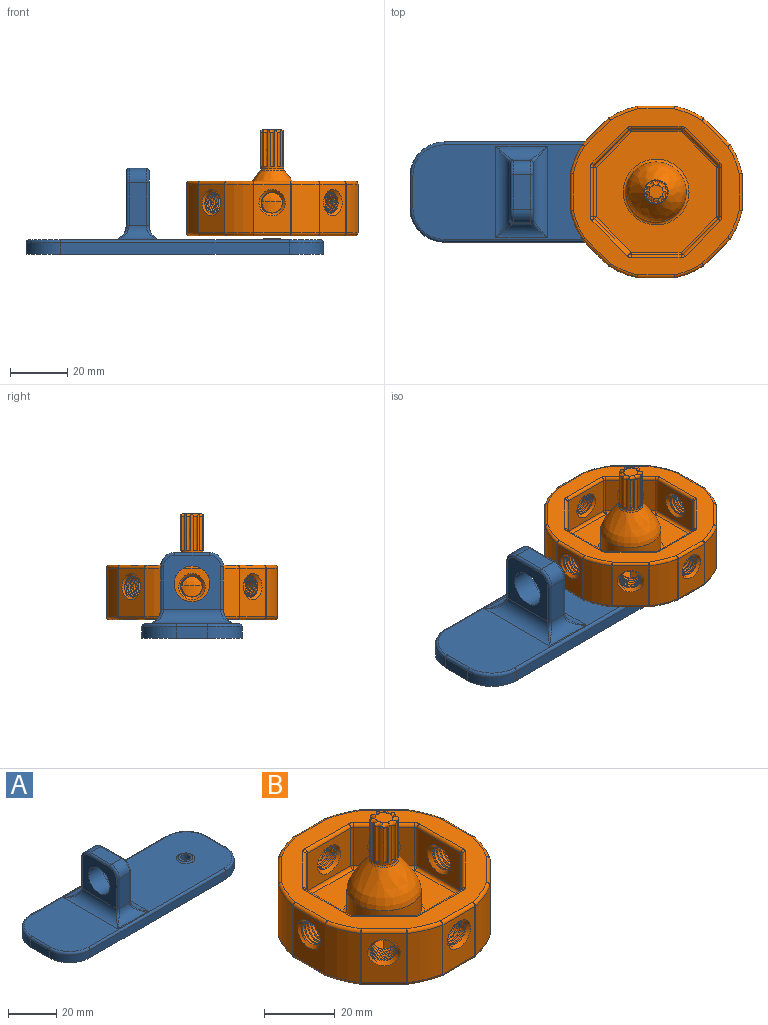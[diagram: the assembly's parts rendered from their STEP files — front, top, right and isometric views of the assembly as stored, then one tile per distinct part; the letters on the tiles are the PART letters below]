
ASSEMBLY  parts=2 mates=1
PART A: 49 faces, bbox 106x37x30.4 mm
  f0: plane 80x4mm, normal (0,1,0), area 320mm2, adj f1,f7,f10,f47
  f1: cylinder r=12mm len=12mm, axis (0,0,-1), area 75.4mm2, adj f0,f2,f10,f45
  f2: plane 11x4mm, normal (-1,0,0), area 44mm2, adj f1,f3,f10,f43
  f3: cylinder r=12mm len=12mm, axis (0,0,-1), area 75.4mm2, adj f2,f4,f10,f41
  f4: plane 80x4mm, normal (0,-1,0), area 320mm2, adj f3,f5,f10,f42
  f5: cylinder r=12mm len=12mm, axis (0,0,-1), area 75.4mm2, adj f4,f6,f10,f44
  f6: plane 11x4mm, normal (1,0,0), area 44mm2, adj f5,f7,f10,f46
  f7: cylinder r=12mm len=12mm, axis (0,0,-1), area 75.4mm2, adj f0,f6,f10,f48
  f8: cylinder r=2mm len=4mm, axis (0,0,-1), area 31.4mm2, adj f11,f13
  f9: plane 102x33mm, normal (0,0,1), area 2639.2mm2, adj f20,f21,f22,f23,f40,f41,f42,f43
  f10: plane 104x35mm, normal (0,0,-1), area 3477.9mm2, adj f0,f1,f2,f3,f4,f5,f6,f7
  f11: plane 6x6mm, normal (0,0,1), area 15.7mm2, adj f8,f40
  f12: cylinder r=3.5mm len=7mm, axis (0,0,-1), area 66mm2, adj f10,f13
  f13: plane 7x7mm, normal (0,0,-1), area 25.9mm2, adj f8,f12
  f14: plane 15x6mm, normal (0,1,0), area 90mm2, adj f23,f25,f31,f38
  f15: plane 20x19mm, normal (-1,0,0), area 250.4mm2, adj f19,f22,f34,f35,f36,f37,f38
  f16: plane 15x6mm, normal (0,-1,0), area 90mm2, adj f20,f24,f27,f34
  f17: plane 20x19mm, normal (1,0,0), area 250.4mm2, adj f19,f21,f27,f28,f29,f30,f31
  f18: plane 12x6mm, normal (0,0,1), area 72mm2, adj f24,f25,f29,f36
  f19: cylinder r=6.25mm len=12.5mm, axis (-1,0,0), area 314.2mm2, adj f15,f17
  f20: cylinder r=5mm len=18mm, axis (-1,0,0), area 81.4mm2, adj f9,f16,f26,f33
  f21: cylinder r=5mm len=32mm, axis (0,-1,0), area 191.3mm2, adj f9,f17,f26,f32
  f22: cylinder r=5mm len=32mm, axis (0,1,0), area 191.3mm2, adj f9,f15,f33,f39
  f23: cylinder r=5mm len=18mm, axis (1,0,0), area 81.4mm2, adj f9,f14,f32,f39
  f24: cylinder r=5mm len=6mm, axis (-1,0,0), area 47.1mm2, adj f16,f18,f28,f35
  f25: cylinder r=5mm len=6mm, axis (1,0,0), area 47.1mm2, adj f14,f18,f30,f37
  f26: bspline ~6x6mm, area 8.8mm2, adj f20,f21,f27
  f27: cylinder r=1mm len=15mm, axis (0,0,1), area 23.6mm2, adj f16,f17,f26,f28
  f28: torus R=4mm, axis (1,0,0), area 11.4mm2, adj f17,f24,f27,f29
  f29: cylinder r=1mm len=12mm, axis (0,-1,0), area 18.8mm2, adj f17,f18,f28,f30
  f30: torus R=4mm, axis (1,0,0), area 11.4mm2, adj f17,f25,f29,f31
  f31: cylinder r=1mm len=15mm, axis (0,0,-1), area 23.6mm2, adj f14,f17,f30,f32
  f32: bspline ~6x6mm, area 8.8mm2, adj f21,f23,f31
  f33: bspline ~6x6mm, area 8.8mm2, adj f20,f22,f34
  f34: cylinder r=1mm len=15mm, axis (0,0,-1), area 23.6mm2, adj f15,f16,f33,f35
  f35: torus R=4mm, axis (1,0,0), area 11.4mm2, adj f15,f24,f34,f36
  f36: cylinder r=1mm len=12mm, axis (0,1,0), area 18.8mm2, adj f15,f18,f35,f37
  f37: torus R=4mm, axis (1,0,0), area 11.4mm2, adj f15,f25,f36,f38
  f38: cylinder r=1mm len=15mm, axis (0,0,1), area 23.6mm2, adj f14,f15,f37,f39
  f39: bspline ~6x6mm, area 8.8mm2, adj f22,f23,f38
  f40: torus R=3.87mm, axis (0,0,1), area 22.3mm2, adj f9,f11
  f41: torus R=11mm, axis (0,0,1), area 28.7mm2, adj f3,f9,f42,f43
  f42: cylinder r=1mm len=80mm, axis (-1,0,0), area 125.7mm2, adj f4,f9,f41,f44
  f43: cylinder r=1mm len=11mm, axis (0,1,0), area 17.3mm2, adj f2,f9,f41,f45
  f44: torus R=11mm, axis (0,0,1), area 28.7mm2, adj f5,f9,f42,f46
  f45: torus R=11mm, axis (0,0,1), area 28.7mm2, adj f1,f9,f43,f47
  f46: cylinder r=1mm len=11mm, axis (0,-1,0), area 17.3mm2, adj f6,f9,f44,f48
  f47: cylinder r=1mm len=80mm, axis (1,0,0), area 125.7mm2, adj f0,f9,f45,f48
  f48: torus R=11mm, axis (0,0,1), area 28.7mm2, adj f7,f9,f46,f47
PART B: 228 faces, bbox 60.9x60.9x37 mm
  f0: cylinder r=4mm len=13.49mm, axis (0,0,1), area 145.4mm2, adj f75,f76,f77,f78,f79,f80,f81,f82
  f1: plane 17.4x13mm, normal (0,-1,0), area 159.7mm2, adj f11,f133,f134,f142,f143
  f2: cylinder r=30.7mm len=17mm, axis (0,0,-1), area 183.4mm2, adj f195,f200,f204,f205
  f3: plane 17x12.78mm, normal (0,1,0), area 150.9mm2, adj f10,f205,f210,f214,f215
  f4: cylinder r=30.7mm len=17mm, axis (0,0,-1), area 183.4mm2, adj f215,f220,f223,f226
  f5: plane 58x58mm, normal (0,0,1), area 970.6mm2, adj f107,f108,f109,f111,f112,f116,f117,f121
  f6: plane 58x58mm, normal (0,0,-1), area 2546.2mm2, adj f153,f154,f163,f164,f173,f174,f183,f184
  f7: cylinder r=6.5mm len=13mm, axis (0,0,-1), area 122.5mm2, adj f74,f227
  f8: plane 42x42mm, normal (0,0,1), area 1045.9mm2, adj f105,f114,f119,f124,f129,f135,f140,f143
  f9: cylinder r=3.6mm len=7.2mm, axis (0,-1,0), area 84.6mm2, adj f10,f11,f12,f13
  f10: cone r=3.6mm half-angle=45deg, axis (0,1,0), area 33.9mm2, adj f3,f9,f12,f13
  f11: cone r=4.6mm half-angle=45deg, axis (0,-1,0), area 33.9mm2, adj f1,f9,f12,f13
  f12: bspline ~8.17x8.17mm, area 57.8mm2, adj f9,f10,f11,f13
  f13: bspline ~8.17x8.17mm, area 57.8mm2, adj f9,f10,f11,f12
  f14: plane 13x12.3mm, normal (-0.71,-0.71,0), area 159.7mm2, adj f19,f122,f123,f134,f135
  f15: cylinder r=30.7mm len=17mm, axis (0,0,-1), area 183.4mm2, adj f175,f180,f184,f185
  f16: plane 17x9.04mm, normal (0.71,0.71,0), area 150.9mm2, adj f18,f185,f190,f194,f195
  f17: cylinder r=3.6mm len=9.33mm, axis (-0.71,-0.71,0), area 84.6mm2, adj f18,f19,f20,f21
  f18: cone r=3.6mm half-angle=45deg, axis (0.71,0.71,0), area 33.9mm2, adj f16,f17,f20,f21
  f19: cone r=4.6mm half-angle=45deg, axis (-0.71,-0.71,0), area 33.9mm2, adj f14,f17,f20,f21
  f20: bspline ~9.75x9.75mm, area 57.8mm2, adj f17,f18,f19,f21
  f21: bspline ~9.75x9.75mm, area 57.8mm2, adj f17,f18,f19,f20
  f22: plane 17.4x13mm, normal (-1,0,0), area 159.7mm2, adj f27,f112,f113,f123,f124
  f23: cylinder r=30.7mm len=17mm, axis (0,0,-1), area 183.4mm2, adj f155,f160,f164,f165
  f24: plane 17x12.78mm, normal (1,0,0), area 150.9mm2, adj f26,f165,f170,f174,f175
  f25: cylinder r=3.6mm len=7.2mm, axis (-1,0,0), area 84.6mm2, adj f26,f27,f28,f29
  f26: cone r=3.6mm half-angle=45deg, axis (1,0,0), area 33.9mm2, adj f24,f25,f28,f29
  f27: cone r=4.6mm half-angle=45deg, axis (-1,0,0), area 33.9mm2, adj f22,f25,f28,f29
  f28: bspline ~8.17x8.17mm, area 57.8mm2, adj f25,f26,f27,f29
  f29: bspline ~8.17x8.17mm, area 57.8mm2, adj f25,f26,f27,f28
  f30: plane 13x12.3mm, normal (-0.71,0.71,0), area 159.7mm2, adj f35,f107,f110,f113,f114
  f31: cylinder r=30.7mm len=17mm, axis (0,0,-1), area 183.4mm2, adj f147,f151,f152,f153
  f32: plane 17x9.04mm, normal (0.71,-0.71,0), area 150.9mm2, adj f34,f147,f150,f154,f155
  f33: cylinder r=3.6mm len=9.33mm, axis (-0.71,0.71,0), area 84.6mm2, adj f34,f35,f36,f37
  f34: cone r=3.6mm half-angle=45deg, axis (0.71,-0.71,0), area 33.9mm2, adj f32,f33,f36,f37
  f35: cone r=4.6mm half-angle=45deg, axis (-0.71,0.71,0), area 33.9mm2, adj f30,f33,f36,f37
  f36: bspline ~9.75x9.75mm, area 57.8mm2, adj f33,f34,f35,f37
  f37: bspline ~9.75x9.75mm, area 57.8mm2, adj f33,f34,f35,f36
  f38: plane 17.4x13mm, normal (0,1,0), area 159.7mm2, adj f43,f110,f111,f119,f120
  f39: cylinder r=30.7mm len=17mm, axis (0,0,-1), area 183.4mm2, adj f162,f171,f172,f173
  f40: plane 17x12.78mm, normal (0,-1,0), area 150.9mm2, adj f42,f152,f161,f162,f163
  f41: cylinder r=3.6mm len=7.2mm, axis (0,1,0), area 84.6mm2, adj f42,f43,f44,f45
  f42: cone r=3.6mm half-angle=45deg, axis (0,-1,0), area 33.9mm2, adj f40,f41,f44,f45
  f43: cone r=4.6mm half-angle=45deg, axis (0,1,0), area 33.9mm2, adj f38,f41,f44,f45
  f44: bspline ~8.17x8.17mm, area 57.8mm2, adj f41,f42,f43,f45
  f45: bspline ~8.17x8.17mm, area 57.8mm2, adj f41,f42,f43,f44
  f46: plane 13x12.3mm, normal (0.71,0.71,0), area 159.7mm2, adj f51,f120,f121,f129,f130
  f47: cylinder r=30.7mm len=17mm, axis (0,0,-1), area 183.4mm2, adj f182,f191,f192,f193
  f48: plane 17x9.04mm, normal (-0.71,-0.71,0), area 150.9mm2, adj f50,f172,f181,f182,f183
  f49: cylinder r=3.6mm len=9.33mm, axis (0.71,0.71,0), area 84.6mm2, adj f50,f51,f52,f53
  f50: cone r=3.6mm half-angle=45deg, axis (-0.71,-0.71,0), area 33.9mm2, adj f48,f49,f52,f53
  f51: cone r=4.6mm half-angle=45deg, axis (0.71,0.71,0), area 33.9mm2, adj f46,f49,f52,f53
  f52: bspline ~9.75x9.75mm, area 57.8mm2, adj f49,f50,f51,f53
  f53: bspline ~9.75x9.75mm, area 57.8mm2, adj f49,f50,f51,f52
  f54: plane 17.4x13mm, normal (1,0,0), area 159.7mm2, adj f59,f130,f131,f140,f141
  f55: cylinder r=30.7mm len=17mm, axis (0,0,-1), area 183.4mm2, adj f202,f211,f212,f213
  f56: plane 17x12.78mm, normal (-1,0,0), area 150.9mm2, adj f58,f192,f201,f202,f203
  f57: cylinder r=3.6mm len=7.2mm, axis (1,0,0), area 84.6mm2, adj f58,f59,f60,f61
  f58: cone r=3.6mm half-angle=45deg, axis (-1,0,0), area 33.9mm2, adj f56,f57,f60,f61
  f59: cone r=4.6mm half-angle=45deg, axis (1,0,0), area 33.9mm2, adj f54,f57,f60,f61
  f60: bspline ~8.17x8.17mm, area 57.8mm2, adj f57,f58,f59,f61
  f61: bspline ~8.17x8.17mm, area 57.8mm2, adj f57,f58,f59,f60
  f62: plane 13x12.3mm, normal (0.71,-0.71,0), area 159.7mm2, adj f66,f132,f141,f142,f146
  f63: plane 17x9.04mm, normal (-0.71,0.71,0), area 150.9mm2, adj f65,f212,f221,f222,f226
  f64: cylinder r=3.6mm len=9.33mm, axis (0.71,-0.71,0), area 84.6mm2, adj f65,f66,f67,f68
  f65: cone r=3.6mm half-angle=45deg, axis (-0.71,0.71,0), area 33.9mm2, adj f63,f64,f67,f68
  f66: cone r=4.6mm half-angle=45deg, axis (0.71,-0.71,0), area 33.9mm2, adj f62,f64,f67,f68
  f67: bspline ~9.75x9.75mm, area 57.8mm2, adj f64,f65,f66,f68
  f68: bspline ~9.75x9.75mm, area 57.8mm2, adj f64,f65,f66,f67
  f69: plane 5.51x5.24mm, normal (0,0,1), area 19.2mm2, adj f95,f96,f97,f98,f99,f100,f101,f102
  f70: revolved ~21x21mm, area 619.2mm2, adj f71,f106
  f71: cylinder r=10.5mm len=21mm, axis (0,0,1), area 468.7mm2, adj f70,f105
  f72: cone r=0mm half-angle=31.2deg, axis (0,0,-1), area 193.9mm2, adj f73
  f73: cylinder r=5.65mm len=11.3mm, axis (0,0,1), area 277mm2, adj f72,f74
  f74: cone r=5.65mm half-angle=45deg, axis (0,0,-1), area 45.9mm2, adj f7,f73
  f75: extruded ~12x1.39mm, area 23.3mm2, adj f0,f76,f100
  f76: plane 1.39x0.99mm, normal (0,0,1), area 0.6mm2, adj f0,f75
  f77: extruded ~12x1.19mm, area 23.3mm2, adj f0,f78,f104
  f78: plane 1.27x1.21mm, normal (0,0,1), area 0.6mm2, adj f0,f77
  f79: extruded ~12x1.39mm, area 23.3mm2, adj f0,f80,f102
  f80: plane 1.39x0.99mm, normal (0,0,1), area 0.6mm2, adj f0,f79
  f81: extruded ~12x1.19mm, area 23.3mm2, adj f0,f82,f98
  f82: plane 1.27x1.21mm, normal (0,0,1), area 0.6mm2, adj f0,f81
  f83: extruded ~12x1.46mm, area 23.3mm2, adj f0,f84,f96
  f84: plane 1.46x0.86mm, normal (0,0,1), area 0.6mm2, adj f0,f83
  f85: extruded ~12x1.19mm, area 23.3mm2, adj f0,f86,f95
  f86: plane 1.27x1.21mm, normal (0,0,1), area 0.6mm2, adj f0,f85
  f87: extruded ~12x1.39mm, area 23.3mm2, adj f0,f88,f97
  f88: plane 1.39x0.99mm, normal (0,0,1), area 0.6mm2, adj f0,f87
  f89: extruded ~12x1.39mm, area 23.3mm2, adj f0,f90,f99
  f90: plane 1.39x0.99mm, normal (0,0,1), area 0.6mm2, adj f0,f89
  f91: extruded ~12x1.19mm, area 23.3mm2, adj f0,f92,f101
  f92: plane 1.27x1.21mm, normal (0,0,1), area 0.6mm2, adj f0,f91
  f93: extruded ~12x1.46mm, area 23.3mm2, adj f0,f94,f103
  f94: plane 1.46x0.86mm, normal (0,0,1), area 0.6mm2, adj f0,f93
  f95: bspline ~2.84x2.54mm, area 3.9mm2, adj f0,f69,f85,f96,f97
  f96: bspline ~3.57x1.98mm, area 3.9mm2, adj f0,f69,f83,f95,f98
  f97: bspline ~3.35x2.26mm, area 3.9mm2, adj f0,f69,f87,f95,f99
  f98: bspline ~3x2.37mm, area 3.9mm2, adj f0,f69,f81,f96,f100
  f99: bspline ~3.35x2.26mm, area 3.9mm2, adj f0,f69,f89,f97,f101
  f100: bspline ~3.35x2.26mm, area 3.9mm2, adj f0,f69,f75,f98,f102
  f101: bspline ~3x2.37mm, area 3.9mm2, adj f0,f69,f91,f99,f103
  f102: bspline ~3.35x2.26mm, area 3.9mm2, adj f0,f69,f79,f100,f104
  f103: bspline ~3.57x1.98mm, area 3.9mm2, adj f0,f69,f93,f101,f104
  f104: bspline ~2.84x2.54mm, area 3.9mm2, adj f0,f69,f77,f102,f103
  f105: torus R=11.5mm, axis (0,0,1), area 107.2mm2, adj f8,f71
  f106: torus R=5mm, axis (0,0,1), area 18.3mm2, adj f0,f70
  f107: cylinder r=1mm len=13.01mm, axis (0.71,0.71,0), area 27.3mm2, adj f5,f30,f108,f109
  f108: torus R=2mm, axis (0,0,1), area 1.7mm2, adj f5,f107,f110,f111
  f109: torus R=2mm, axis (0,0,1), area 1.7mm2, adj f5,f107,f112,f113
  f110: cylinder r=1mm len=13mm, axis (0,0,1), area 10.2mm2, adj f30,f38,f108,f115
  f111: cylinder r=1mm len=17.4mm, axis (1,0,0), area 27.3mm2, adj f5,f38,f108,f116
  f112: cylinder r=1mm len=17.4mm, axis (0,1,0), area 27.3mm2, adj f5,f22,f109,f117
  f113: cylinder r=1mm len=13mm, axis (0,0,1), area 10.2mm2, adj f22,f30,f109,f118
  f114: cylinder r=1mm len=13.01mm, axis (-0.71,-0.71,0), area 27.3mm2, adj f8,f30,f115,f118
  f115: sphere r=1mm, area 0.8mm2, adj f110,f114,f119
  f116: torus R=2mm, axis (0,0,1), area 1.7mm2, adj f5,f111,f120,f121
  f117: torus R=2mm, axis (0,0,1), area 1.7mm2, adj f5,f112,f122,f123
  f118: sphere r=1mm, area 0.8mm2, adj f113,f114,f124
  f119: cylinder r=1mm len=17.4mm, axis (-1,0,0), area 27.3mm2, adj f8,f38,f115,f125
  f120: cylinder r=1mm len=13mm, axis (0,0,1), area 10.2mm2, adj f38,f46,f116,f125
  f121: cylinder r=1mm len=13.01mm, axis (0.71,-0.71,0), area 27.3mm2, adj f5,f46,f116,f126
  f122: cylinder r=1mm len=13.01mm, axis (-0.71,0.71,0), area 27.3mm2, adj f5,f14,f117,f127
  f123: cylinder r=1mm len=13mm, axis (0,0,1), area 10.2mm2, adj f14,f22,f117,f128
  f124: cylinder r=1mm len=17.4mm, axis (0,-1,0), area 27.3mm2, adj f8,f22,f118,f128
  f125: sphere r=1mm, area 0.8mm2, adj f119,f120,f129
  f126: torus R=2mm, axis (0,0,1), area 1.7mm2, adj f5,f121,f130,f131
  f127: torus R=2mm, axis (0,0,1), area 1.7mm2, adj f5,f122,f133,f134
  f128: sphere r=1mm, area 0.8mm2, adj f123,f124,f135
  f129: cylinder r=1mm len=13.01mm, axis (-0.71,0.71,0), area 27.3mm2, adj f8,f46,f125,f136
  f130: cylinder r=1mm len=13mm, axis (0,0,1), area 10.2mm2, adj f46,f54,f126,f136
  f131: cylinder r=1mm len=17.4mm, axis (0,-1,0), area 27.3mm2, adj f5,f54,f126,f137
  f132: cylinder r=1mm len=13.01mm, axis (-0.71,-0.71,0), area 27.3mm2, adj f5,f62,f137,f138
  f133: cylinder r=1mm len=17.4mm, axis (-1,0,0), area 27.3mm2, adj f1,f5,f127,f138
  f134: cylinder r=1mm len=13mm, axis (0,0,1), area 10.2mm2, adj f1,f14,f127,f139
  f135: cylinder r=1mm len=13.01mm, axis (0.71,-0.71,0), area 27.3mm2, adj f8,f14,f128,f139
  f136: sphere r=1mm, area 0.5mm2, adj f129,f130,f140
  f137: torus R=2mm, axis (0,0,1), area 1.7mm2, adj f5,f131,f132,f141
  f138: torus R=2mm, axis (0,0,1), area 1.7mm2, adj f5,f132,f133,f142
  f139: sphere r=1mm, area 1.1mm2, adj f134,f135,f143
  f140: cylinder r=1mm len=17.4mm, axis (0,1,0), area 27.3mm2, adj f8,f54,f136,f144
  f141: cylinder r=1mm len=13mm, axis (0,0,1), area 10.2mm2, adj f54,f62,f137,f144
  f142: cylinder r=1mm len=13mm, axis (0,0,1), area 10.2mm2, adj f1,f62,f138,f145
  f143: cylinder r=1mm len=17.4mm, axis (1,0,0), area 27.3mm2, adj f1,f8,f139,f145
  f144: sphere r=1mm, area 0.8mm2, adj f140,f141,f146
  f145: sphere r=1mm, area 0.8mm2, adj f142,f143,f146
  f146: cylinder r=1mm len=13.01mm, axis (0.71,0.71,0), area 27.3mm2, adj f8,f62,f144,f145
  f147: cylinder r=1mm len=17mm, axis (0,0,-1), area 3.7mm2, adj f31,f32,f148,f149
  f148: sphere r=1mm, area 0.2mm2, adj f147,f150,f151
  f149: sphere r=1mm, area 0.2mm2, adj f147,f153,f154
  f150: cylinder r=1mm len=9.75mm, axis (-0.71,-0.71,0), area 20.1mm2, adj f5,f32,f148,f156
  f151: torus R=29.7mm, axis (0,0,1), area 16.7mm2, adj f5,f31,f148,f157
  f152: cylinder r=1mm len=17mm, axis (0,0,-1), area 3.7mm2, adj f31,f40,f157,f158
  f153: torus R=29.7mm, axis (0,0,1), area 16.7mm2, adj f6,f31,f149,f158
  f154: cylinder r=1mm len=9.75mm, axis (0.71,0.71,0), area 20.1mm2, adj f6,f32,f149,f159
  f155: cylinder r=1mm len=17mm, axis (0,0,-1), area 3.7mm2, adj f23,f32,f156,f159
  f156: sphere r=1mm, area 0.2mm2, adj f150,f155,f160
  f157: sphere r=1mm, area 0.2mm2, adj f151,f152,f161
  f158: sphere r=1mm, area 0.2mm2, adj f152,f153,f163
  f159: sphere r=1mm, area 0.2mm2, adj f154,f155,f164
  f160: torus R=29.7mm, axis (0,0,1), area 16.7mm2, adj f5,f23,f156,f166
  f161: cylinder r=1mm len=12.78mm, axis (-1,0,0), area 20.1mm2, adj f5,f40,f157,f167
  f162: cylinder r=1mm len=17mm, axis (0,0,-1), area 3.7mm2, adj f39,f40,f167,f168
  f163: cylinder r=1mm len=12.78mm, axis (1,0,0), area 20.1mm2, adj f6,f40,f158,f168
  f164: torus R=29.7mm, axis (0,0,1), area 16.7mm2, adj f6,f23,f159,f169
  f165: cylinder r=1mm len=17mm, axis (0,0,-1), area 3.7mm2, adj f23,f24,f166,f169
  f166: sphere r=1mm, area 0.2mm2, adj f160,f165,f170
  f167: sphere r=1mm, area 0.2mm2, adj f161,f162,f171
  f168: sphere r=1mm, area 0.2mm2, adj f162,f163,f173
  f169: sphere r=1mm, area 0.2mm2, adj f164,f165,f174
  f170: cylinder r=1mm len=12.78mm, axis (0,-1,0), area 20.1mm2, adj f5,f24,f166,f176
  f171: torus R=29.7mm, axis (0,0,1), area 16.7mm2, adj f5,f39,f167,f177
  f172: cylinder r=1mm len=17mm, axis (0,0,-1), area 3.7mm2, adj f39,f48,f177,f178
  f173: torus R=29.7mm, axis (0,0,1), area 16.7mm2, adj f6,f39,f168,f178
  f174: cylinder r=1mm len=12.78mm, axis (0,1,0), area 20.1mm2, adj f6,f24,f169,f179
  f175: cylinder r=1mm len=17mm, axis (0,0,-1), area 3.7mm2, adj f15,f24,f176,f179
  f176: sphere r=1mm, area 0.2mm2, adj f170,f175,f180
  f177: sphere r=1mm, area 0.2mm2, adj f171,f172,f181
  f178: sphere r=1mm, area 0.2mm2, adj f172,f173,f183
  f179: sphere r=1mm, area 0.1mm2, adj f174,f175,f184
  f180: torus R=29.7mm, axis (0,0,1), area 16.7mm2, adj f5,f15,f176,f186
  f181: cylinder r=1mm len=9.75mm, axis (-0.71,0.71,0), area 20.1mm2, adj f5,f48,f177,f187
  f182: cylinder r=1mm len=17mm, axis (0,0,-1), area 3.7mm2, adj f47,f48,f187,f188
  f183: cylinder r=1mm len=9.75mm, axis (0.71,-0.71,0), area 20.1mm2, adj f6,f48,f178,f188
  f184: torus R=29.7mm, axis (0,0,1), area 16.7mm2, adj f6,f15,f179,f189
  f185: cylinder r=1mm len=17mm, axis (0,0,-1), area 3.7mm2, adj f15,f16,f186,f189
  f186: sphere r=1mm, area 0.2mm2, adj f180,f185,f190
  f187: sphere r=1mm, area 0.2mm2, adj f181,f182,f191
  f188: sphere r=1mm, area 0.2mm2, adj f182,f183,f193
  f189: sphere r=1mm, area 0.2mm2, adj f184,f185,f194
  f190: cylinder r=1mm len=9.75mm, axis (0.71,-0.71,0), area 20.1mm2, adj f5,f16,f186,f196
  f191: torus R=29.7mm, axis (0,0,1), area 16.7mm2, adj f5,f47,f187,f197
  f192: cylinder r=1mm len=17mm, axis (0,0,-1), area 3.7mm2, adj f47,f56,f197,f198
  f193: torus R=29.7mm, axis (0,0,1), area 16.7mm2, adj f6,f47,f188,f198
  f194: cylinder r=1mm len=9.75mm, axis (-0.71,0.71,0), area 20.1mm2, adj f6,f16,f189,f199
  f195: cylinder r=1mm len=17mm, axis (0,0,-1), area 3.7mm2, adj f2,f16,f196,f199
  f196: sphere r=1mm, area 0.2mm2, adj f190,f195,f200
  f197: sphere r=1mm, area 0.2mm2, adj f191,f192,f201
  f198: sphere r=1mm, area 0.2mm2, adj f192,f193,f203
  f199: sphere r=1mm, area 0.2mm2, adj f194,f195,f204
  f200: torus R=29.7mm, axis (0,0,1), area 16.7mm2, adj f2,f5,f196,f206
  f201: cylinder r=1mm len=12.78mm, axis (0,1,0), area 20.1mm2, adj f5,f56,f197,f207
  f202: cylinder r=1mm len=17mm, axis (0,0,-1), area 3.7mm2, adj f55,f56,f207,f208
  f203: cylinder r=1mm len=12.78mm, axis (0,-1,0), area 20.1mm2, adj f6,f56,f198,f208
  f204: torus R=29.7mm, axis (0,0,1), area 16.7mm2, adj f2,f6,f199,f209
  f205: cylinder r=1mm len=17mm, axis (0,0,-1), area 3.7mm2, adj f2,f3,f206,f209
  f206: sphere r=1mm, area 0.2mm2, adj f200,f205,f210
  f207: sphere r=1mm, area 0.2mm2, adj f201,f202,f211
  f208: sphere r=1mm, area 0.2mm2, adj f202,f203,f213
  f209: sphere r=1mm, area 0.2mm2, adj f204,f205,f214
  f210: cylinder r=1mm len=12.78mm, axis (1,0,0), area 20.1mm2, adj f3,f5,f206,f216
  f211: torus R=29.7mm, axis (0,0,1), area 16.7mm2, adj f5,f55,f207,f217
  f212: cylinder r=1mm len=17mm, axis (0,0,-1), area 3.7mm2, adj f55,f63,f217,f218
  f213: torus R=29.7mm, axis (0,0,1), area 16.7mm2, adj f6,f55,f208,f218
  f214: cylinder r=1mm len=12.78mm, axis (-1,0,0), area 20.1mm2, adj f3,f6,f209,f219
  f215: cylinder r=1mm len=17mm, axis (0,0,-1), area 3.7mm2, adj f3,f4,f216,f219
  f216: sphere r=1mm, area 0.2mm2, adj f210,f215,f220
  f217: sphere r=1mm, area 0.2mm2, adj f211,f212,f221
  f218: sphere r=1mm, area 0.2mm2, adj f212,f213,f222
  f219: sphere r=1mm, area 0.2mm2, adj f214,f215,f223
  f220: torus R=29.7mm, axis (0,0,1), area 16.7mm2, adj f4,f5,f216,f224
  f221: cylinder r=1mm len=9.75mm, axis (0.71,0.71,0), area 20.1mm2, adj f5,f63,f217,f224
  f222: cylinder r=1mm len=9.75mm, axis (-0.71,-0.71,0), area 20.1mm2, adj f6,f63,f218,f225
  f223: torus R=29.7mm, axis (0,0,1), area 16.7mm2, adj f4,f6,f219,f225
  f224: sphere r=1mm, area 0.2mm2, adj f220,f221,f226
  f225: sphere r=1mm, area 0.2mm2, adj f222,f223,f226
  f226: cylinder r=1mm len=17mm, axis (0,0,-1), area 3.7mm2, adj f4,f63,f224,f225
  f227: torus R=7.5mm, axis (0,0,1), area 67.7mm2, adj f6,f7
PLACE A at identity fixed
PLACE B t=(0,0,6.5)mm
MATE revolute B.f23 <-> A.f40  axis (0,0,-1) through (0,0,6.5)mm
